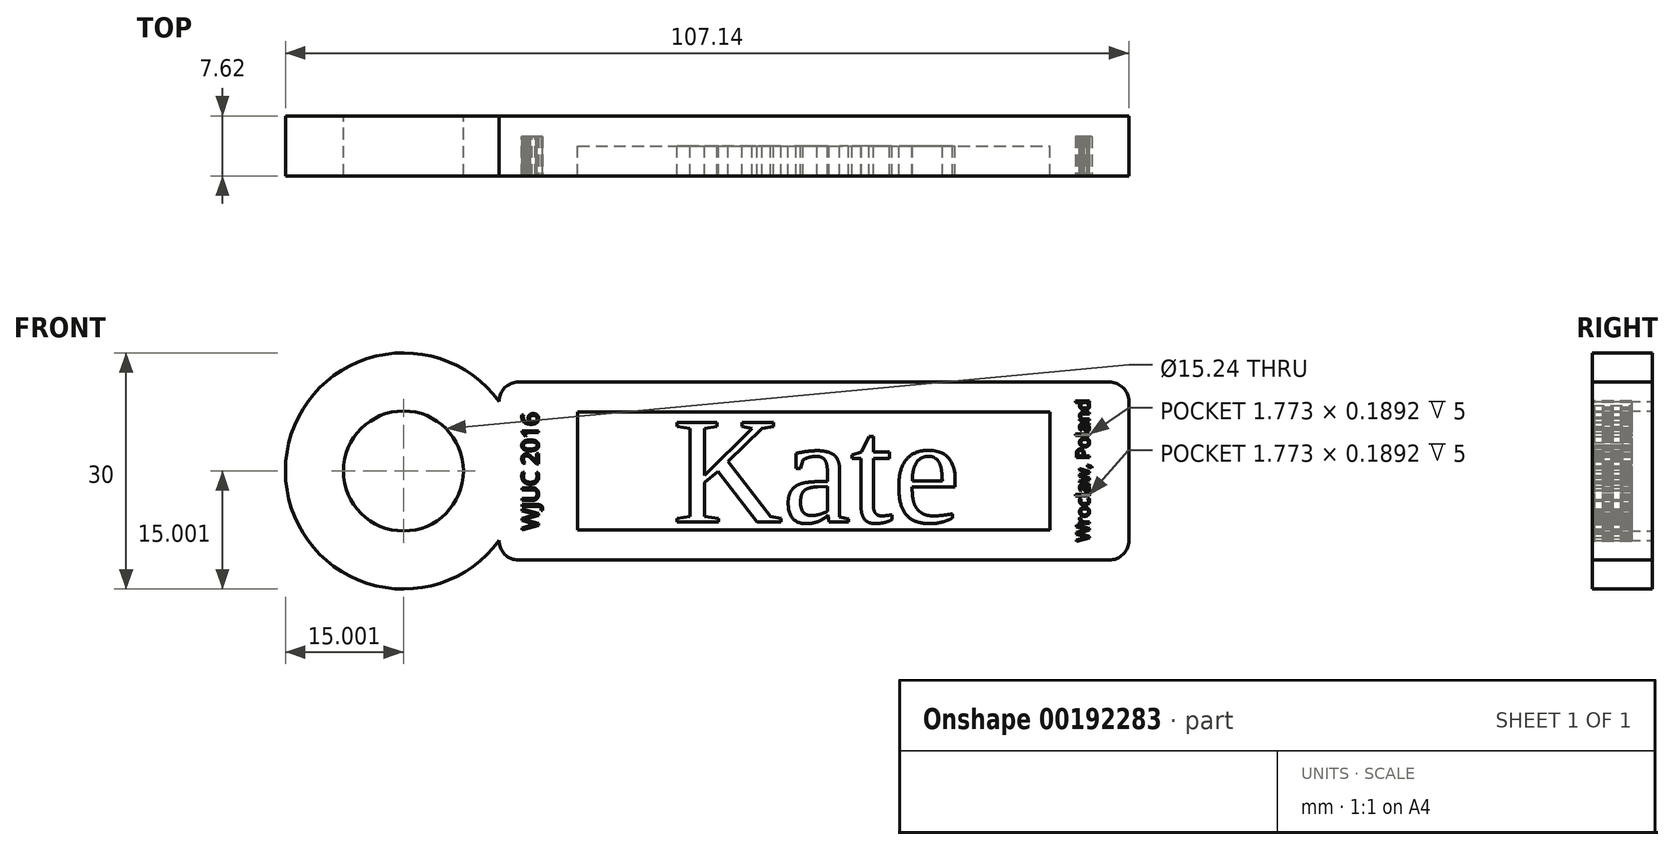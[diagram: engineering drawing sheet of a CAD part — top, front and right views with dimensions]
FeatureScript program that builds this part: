
annotation { "Feature Type Name" : "Feature", "Feature Type Description" : "" }
export const myFeature = defineFeature(function(context is Context, id is Id, definition is map)
    precondition{}
    {
        {
            var Q0;
            Q0=qCreatedBy(makeId("Front.planeOp"),FACE);
            var sketch = newSketch(context, id + "F0", { "sketchPlane" : qUnion([Q0])});
            skLineSegment(sketch, "E0.bottom", {"start": v(15.9, -22.64) * mm, "end": v(-59.1, -22.64) * mm});
            skLineSegment(sketch, "E0.top", {"start": v(15.9, 0) * mm, "end": v(-59.1, 0) * mm});
            skLineSegment(sketch, "E0.left", {"start": v(18.4, -20.14) * mm, "end": v(18.4, -2.5) * mm});
            skLineSegment(sketch, "E0.right", {"start": v(-61.6, -20.14) * mm, "end": v(-61.6, -2.5) * mm});
            skPoint(sketch, "E1.visualSharp", {"position": v(-61.6, 0) * mm});
            skArc(sketch, "E1.filletArc", {"start": v(-59.1, 0) * mm, "mid": v(-60.87, -0.73) * mm, "end": v(-61.6, -2.5) * mm});
            skPoint(sketch, "E2.visualSharp", {"position": v(-61.6, -22.64) * mm});
            skArc(sketch, "E2.filletArc", {"start": v(-61.6, -20.14) * mm, "mid": v(-60.87, -21.9) * mm, "end": v(-59.1, -22.64) * mm});
            skPoint(sketch, "E3.visualSharp", {"position": v(18.4, -22.64) * mm});
            skArc(sketch, "E3.filletArc", {"start": v(15.9, -22.64) * mm, "mid": v(17.66, -21.9) * mm, "end": v(18.4, -20.14) * mm});
            skPoint(sketch, "E4.visualSharp", {"position": v(18.4, 0) * mm});
            skArc(sketch, "E4.filletArc", {"start": v(18.4, -2.5) * mm, "mid": v(17.66, -0.73) * mm, "end": v(15.9, 0) * mm});
            skArc(sketch, "E5", {"start": v(-61.6, -2.5) * mm, "mid": v(-88.74, -11.32) * mm, "end": v(-61.6, -20.14) * mm});
            skSolve(sketch);
        }
        {
            var Q0;
            Q0=makeQuery(id+"F0.imprint","IMPRINT",FACE,{"disambiguationData":[TD([[makeQuery(id+"F0.imprint","IMPRINT",EDGE,{"derivedFrom":sQuery(id+"F0.wireOp",EDGE,"E0.bottom")}),-1.0]])]});
            extrude(context, id + "F1", {"entities" : qUnion([Q0]), "depth" : 3.8 * mm});
        }
        {
            var Q0;
            Q0=makeQuery(id+"F0.imprint","IMPRINT",FACE,{"disambiguationData":[TD([[makeQuery(id+"F0.imprint","IMPRINT",EDGE,{"derivedFrom":sQuery(id+"F0.wireOp",EDGE,"E0.right")}),1.0]])]});
            extrude(context, id + "F2", {"entities" : qUnion([Q0]), "operationType" : NewBodyOperationType.ADD, "depth" : 3.8 * mm});
        }
        {
            var Q0;
            Q0=sQuery(id+"F0.wireOp",VERTEX,"E5.center");
            var Q1;
            Q1=makeQuery(id+"F1.opExtrude","SWEPT_BODY",BODY,{"disambiguationData":[OSD([sQuery(id+"F0.wireOp",EDGE,"E0.bottom"),sQuery(id+"F0.wireOp",EDGE,"E0.top"),sQuery(id+"F0.wireOp",EDGE,"E0.left"),sQuery(id+"F0.wireOp",EDGE,"E0.right"),sQuery(id+"F0.wireOp",EDGE,"E1.filletArc"),sQuery(id+"F0.wireOp",EDGE,"E2.filletArc"),sQuery(id+"F0.wireOp",EDGE,"E3.filletArc"),sQuery(id+"F0.wireOp",EDGE,"E4.filletArc")])]});
            hole(context, id + "F3", {"style" : HoleStyle.SIMPLE, "holeDiameter" : 12.7 * mm, "endStyle" : HoleEndStyle.THROUGH, "oppositeDirection" : true, "locations" : qUnion([Q0]), "scope" : qUnion([Q1])});
        }
        {
            var Q0;
            {var subQ0=sQuery(id+"F0.wireOp",EDGE,"E0.right");Q0=makeQuery(id+"F2.boolean.opBoolean","MERGE",FACE,{"derivedFrom":[makeQuery(id+"F1.opExtrude","CAP_FACE",FACE,{"disambiguationData":[OSD([sQuery(id+"F0.wireOp",EDGE,"E0.bottom"),sQuery(id+"F0.wireOp",EDGE,"E0.top"),sQuery(id+"F0.wireOp",EDGE,"E0.left"),subQ0,sQuery(id+"F0.wireOp",EDGE,"E1.filletArc"),sQuery(id+"F0.wireOp",EDGE,"E2.filletArc"),sQuery(id+"F0.wireOp",EDGE,"E3.filletArc"),sQuery(id+"F0.wireOp",EDGE,"E4.filletArc")])],"isStart":false}),makeQuery(id+"F2.opExtrude","CAP_FACE",FACE,{"disambiguationData":[OSD([subQ0,sQuery(id+"F0.wireOp",EDGE,"E5")])],"isStart":false})]});}
            var sketch = newSketch(context, id + "F4", { "sketchPlane" : qUnion([Q0])});
            skLineSegment(sketch, "E6.bottom", {"start": v(-51.6, -3.82) * mm, "end": v(8.4, -3.82) * mm});
            skLineSegment(sketch, "E6.top", {"start": v(-51.6, -18.82) * mm, "end": v(8.4, -18.82) * mm});
            skLineSegment(sketch, "E6.left", {"start": v(-51.6, -3.82) * mm, "end": v(-51.6, -18.82) * mm});
            skLineSegment(sketch, "E6.right", {"start": v(8.4, -3.82) * mm, "end": v(8.4, -18.82) * mm});
            skSolve(sketch);
        }
        {
            var Q0;
            Q0=makeQuery(id+"F4.imprint","IMPRINT",FACE,{"disambiguationData":[TD([[makeQuery(id+"F4.imprint","IMPRINT",EDGE,{"derivedFrom":sQuery(id+"F4.wireOp",EDGE,"E6.bottom")}),1.0]])]});
            extrude(context, id + "F5", {"entities" : qUnion([Q0]), "operationType" : NewBodyOperationType.ADD, "depth" : 3.8 * mm});
        }
        {
            var Q0;
            Q0=qCreatedBy(makeId("Front.planeOp"),FACE);
            var sketch = newSketch(context, id + "F6", { "sketchPlane" : qUnion([Q0])});
            skText(sketch, "E7", { "text": "Kate", "fontName": "Tinos-Regular.ttf"});
            const initialGuessF6  = {"E7": [-0.03954, -0.01782, 1, 0, 0.01394]};
            skSetInitialGuess(sketch, initialGuessF6);
            skSolve(sketch);
        }
        {
            var Q0;
            Q0=qSketchRegion(id+"F6",true);
            extrude(context, id + "F7", {"entities" : qUnion([Q0]), "operationType" : NewBodyOperationType.ADD, "depth" : 3.8 * mm});
        }
        {
            var Q0;
            Q0=qSketchRegion(id+"F6",true);
            var Q1;
            Q1=makeQuery(id+"F0.imprint","IMPRINT",FACE,{"disambiguationData":[TD([[makeQuery(id+"F0.imprint","IMPRINT",EDGE,{"derivedFrom":sQuery(id+"F0.wireOp",EDGE,"E0.right")}),1.0]])]});
            var Q2;
            Q2=makeQuery(id+"F5.opExtrude","CAP_FACE",FACE,{"disambiguationData":[OSD([sQuery(id+"F0.wireOp",EDGE,"E0.bottom"),sQuery(id+"F0.wireOp",EDGE,"E0.top"),sQuery(id+"F0.wireOp",EDGE,"E0.left"),sQuery(id+"F0.wireOp",EDGE,"E0.right"),sQuery(id+"F0.wireOp",EDGE,"E1.filletArc"),sQuery(id+"F0.wireOp",EDGE,"E2.filletArc"),sQuery(id+"F0.wireOp",EDGE,"E3.filletArc"),sQuery(id+"F0.wireOp",EDGE,"E4.filletArc"),sQuery(id+"F0.wireOp",EDGE,"E5"),sQuery(id+"F3.hole-0.sketch.wireOp",EDGE,"core_line_2"),sQuery(id+"F4.wireOp",EDGE,"E6.bottom"),sQuery(id+"F4.wireOp",EDGE,"E6.top"),sQuery(id+"F4.wireOp",EDGE,"E6.left"),sQuery(id+"F4.wireOp",EDGE,"E6.right")])],"isStart":false});
            extrude(context, id + "F8", {"entities" : qUnion([Q0, Q1]), "operationType" : NewBodyOperationType.ADD, "endBound" : BoundingType.UP_TO_SURFACE, "endBoundEntityFace" : qUnion([Q2]), "depth" : 3.8 * mm});
        }
        {
            var Q0;
            Q0=sQuery(id+"F0.wireOp",VERTEX,"E5.center");
            var Q1;
            Q1=makeQuery(id+"F1.opExtrude","SWEPT_BODY",BODY,{"disambiguationData":[OSD([sQuery(id+"F0.wireOp",EDGE,"E0.bottom"),sQuery(id+"F0.wireOp",EDGE,"E0.top"),sQuery(id+"F0.wireOp",EDGE,"E0.left"),sQuery(id+"F0.wireOp",EDGE,"E0.right"),sQuery(id+"F0.wireOp",EDGE,"E1.filletArc"),sQuery(id+"F0.wireOp",EDGE,"E2.filletArc"),sQuery(id+"F0.wireOp",EDGE,"E3.filletArc"),sQuery(id+"F0.wireOp",EDGE,"E4.filletArc")])]});
            hole(context, id + "F9", {"style" : HoleStyle.SIMPLE, "holeDiameter" : 15.24 * mm, "endStyle" : HoleEndStyle.THROUGH, "oppositeDirection" : true, "locations" : qUnion([Q0]), "scope" : qUnion([Q1])});
        }
        {
            var Q0;
            {var subQ0=sQuery(id+"F0.wireOp",EDGE,"E5");var subQ1=sQuery(id+"F0.wireOp",EDGE,"E0.right");var subQ2=sQuery(id+"F4.wireOp",EDGE,"E6.right");var subQ3=sQuery(id+"F4.wireOp",EDGE,"E6.left");var subQ4=sQuery(id+"F4.wireOp",EDGE,"E6.top");var subQ5=sQuery(id+"F4.wireOp",EDGE,"E6.bottom");var subQ6=sQuery(id+"F3.hole-0.sketch.wireOp",EDGE,"core_line_2");var subQ7=sQuery(id+"F0.wireOp",EDGE,"E4.filletArc");var subQ8=sQuery(id+"F0.wireOp",EDGE,"E3.filletArc");var subQ9=sQuery(id+"F0.wireOp",EDGE,"E2.filletArc");var subQ10=sQuery(id+"F0.wireOp",EDGE,"E1.filletArc");var subQ11=sQuery(id+"F0.wireOp",EDGE,"E0.left");var subQ12=sQuery(id+"F0.wireOp",EDGE,"E0.top");var subQ13=sQuery(id+"F0.wireOp",EDGE,"E0.bottom");Q0=makeQuery(id+"F8.boolean.opBoolean","MERGE",FACE,{"derivedFrom":[makeQuery(id+"F5.opExtrude","CAP_FACE",FACE,{"disambiguationData":[OSD([subQ13,subQ12,subQ11,subQ1,subQ10,subQ9,subQ8,subQ7,subQ0,subQ6,subQ5,subQ4,subQ3,subQ2])],"isStart":false}),makeQuery(id+"F8.opExtrude","CAP_FACE",FACE,{"disambiguationData":[OSD([subQ13,subQ12,subQ11,subQ1,subQ10,subQ9,subQ8,subQ7,subQ0,subQ6,subQ5,subQ4,subQ3,subQ2]),ownerDisambiguation([makeQuery(id+"F8.opExtrude","SWEPT_BODY",BODY,{"disambiguationData":[OSD([subQ1,subQ0])]})])],"isStart":false})]});}
            var sketch = newSketch(context, id + "F10", { "sketchPlane" : qUnion([Q0])});
            skText(sketch, "E8", { "text": "WJUC 2016", "fontName": "OpenSans-Regular.ttf"});
            const initialGuessF10  = {"E8": [-0.0566, -0.01882, 0, 1, 0.00211]};
            skSetInitialGuess(sketch, initialGuessF10);
            skSolve(sketch);
        }
        {
            var Q0;
            Q0 = qSketchRegion(id + "F10", true);
            extrude(context, id + "F11", {"entities" : qUnion([Q0]), "operationType" : NewBodyOperationType.REMOVE, "oppositeDirection" : true, "depth" : 5 * mm});
        }
        {
            var Q0;
            {var subQ0=sQuery(id+"F0.wireOp",EDGE,"E5");var subQ1=sQuery(id+"F0.wireOp",EDGE,"E4.filletArc");var subQ2=sQuery(id+"F0.wireOp",EDGE,"E2.filletArc");var subQ3=sQuery(id+"F0.wireOp",EDGE,"E0.left");var subQ4=sQuery(id+"F4.wireOp",EDGE,"E6.top");var subQ5=sQuery(id+"F4.wireOp",EDGE,"E6.bottom");var subQ6=sQuery(id+"F0.wireOp",EDGE,"E0.top");var subQ7=sQuery(id+"F4.wireOp",EDGE,"E6.left");var subQ8=sQuery(id+"F0.wireOp",EDGE,"E3.filletArc");var subQ9=sQuery(id+"F0.wireOp",EDGE,"E1.filletArc");var subQ10=sQuery(id+"F0.wireOp",EDGE,"E0.bottom");var subQ11=sQuery(id+"F4.wireOp",EDGE,"E6.right");var subQ12=sQuery(id+"F0.wireOp",EDGE,"E0.right");var subQ13=sQuery(id+"F3.hole-0.sketch.wireOp",EDGE,"core_line_2");Q0=makeQuery(id+"F11.boolean.opBoolean","SPLIT",FACE,{"disambiguationData":[TD([makeQuery(id+"F1.opExtrude","SWEPT_FACE",FACE,{"disambiguationData":[OSD([subQ10])]})])],"derivedFrom":makeQuery(id+"F8.boolean.opBoolean","MERGE",FACE,{"derivedFrom":[makeQuery(id+"F5.opExtrude","CAP_FACE",FACE,{"disambiguationData":[OSD([subQ10,subQ6,subQ3,subQ12,subQ9,subQ2,subQ8,subQ1,subQ0,subQ13,subQ5,subQ4,subQ7,subQ11])],"isStart":false}),makeQuery(id+"F8.opExtrude","CAP_FACE",FACE,{"disambiguationData":[OSD([subQ10,subQ6,subQ3,subQ12,subQ9,subQ2,subQ8,subQ1,subQ0,subQ13,subQ5,subQ4,subQ7,subQ11]),ownerDisambiguation([makeQuery(id+"F8.opExtrude","SWEPT_BODY",BODY,{"disambiguationData":[OSD([subQ12,subQ0])]})])],"isStart":false})]})});}
            var sketch = newSketch(context, id + "F12", { "sketchPlane" : qUnion([Q0])});
            skText(sketch, "E9", { "text": "Wroclaw, Poland", "fontName": "OpenSans-Regular.ttf"});
            const initialGuessF12  = {"E9": [0.0134, -0.02032, 0, 1, 0.00168]};
            skSetInitialGuess(sketch, initialGuessF12);
            skSolve(sketch);
        }
        {
            var Q0;
            Q0 = qSketchRegion(id + "F12", true);
            extrude(context, id + "F13", {"entities" : qUnion([Q0]), "operationType" : NewBodyOperationType.REMOVE, "oppositeDirection" : true, "depth" : 5 * mm});
        }
    });
